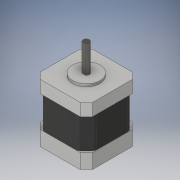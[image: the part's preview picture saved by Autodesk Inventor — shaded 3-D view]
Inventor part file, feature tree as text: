
AUTODESK INVENTOR PART (.ipt)
format: ipt  version: 2019 (Build 230136000, 136)  size: 226,304 bytes
history: native  units: mm
features: extrude x7, sketch x7, other x1, fillet x1, chamfer x1, projected_geometry x1
ambient origin geometry x8: Origin, YZ Plane, XZ Plane, XY Plane, X Axis, Y Axis, Z Axis, Center Point
bodies: Body1 (feature_tree)
feature tree (18):
  other  "Твердое тело1"
  extrude  "Выдавливание1"  Depth=42.3mm
  extrude  "Выдавливание2"  Depth=5.0mm
  extrude  "Выдавливание3"  Depth=5.0mm
  fillet  "Сопряжение1"  Radius=5.0mm
  extrude  "Выдавливание4"  Depth=5.0mm
  extrude  "Выдавливание5"  Depth=5.0mm
  extrude  "Выдавливание6"  Depth=5.0mm
  extrude  "Выдавливание8"  Depth=5.0mm
  chamfer  "Фаска1"  Distance=5.0mm
  sketch  "Эскиз1"
  sketch  "Эскиз2"
  sketch  "Эскиз3"
  projected_geometry  "Спроецированная петля1"
  sketch  "Эскиз4"
  sketch  "Эскиз5"
  sketch  "Эскиз6"
  sketch  "Эскиз9"
